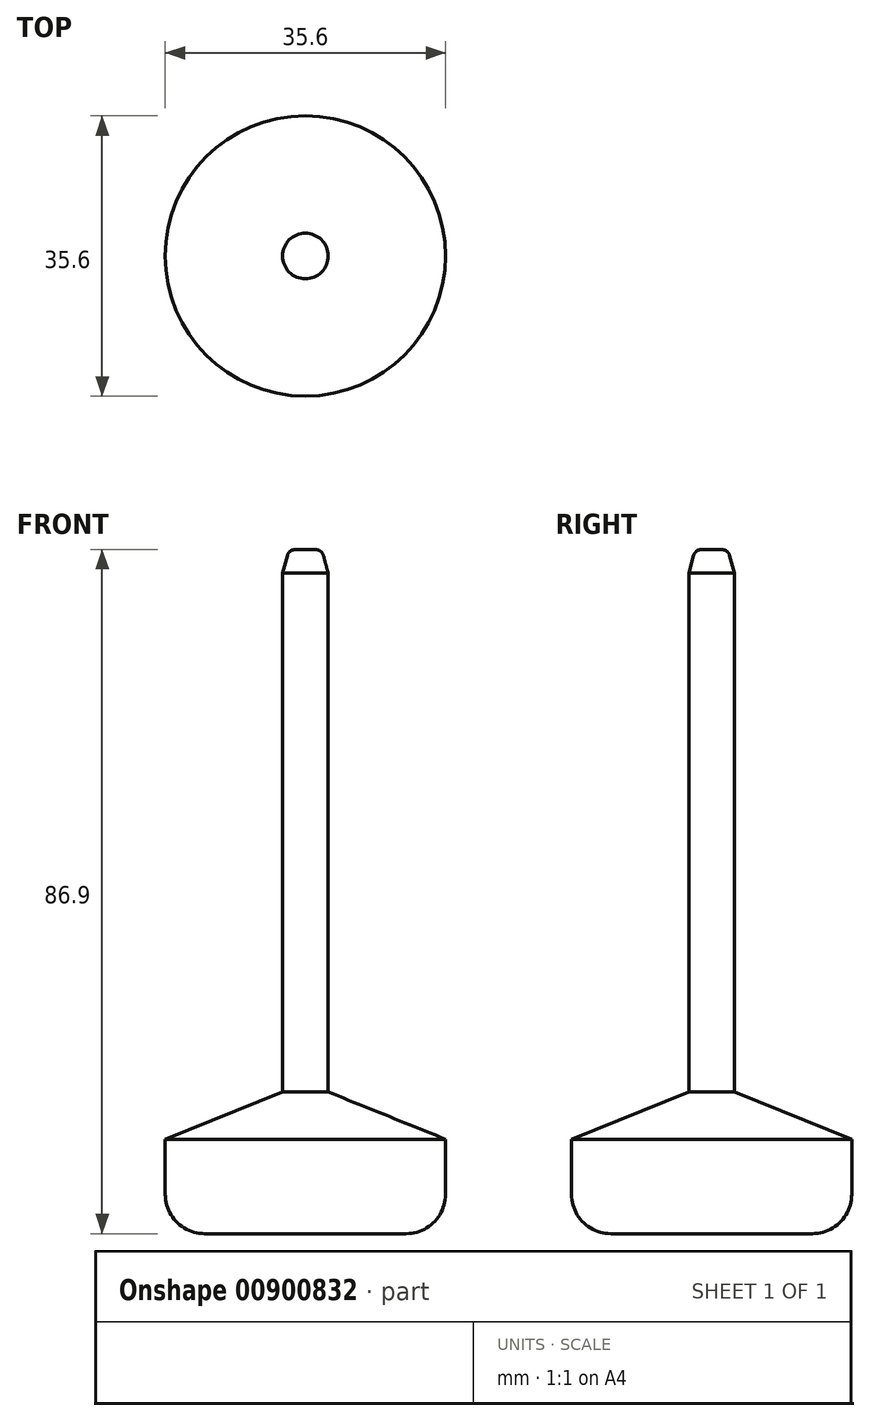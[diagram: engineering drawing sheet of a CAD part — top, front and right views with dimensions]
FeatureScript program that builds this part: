
annotation { "Feature Type Name" : "Feature", "Feature Type Description" : "" }
export const myFeature = defineFeature(function(context is Context, id is Id, definition is map)
    precondition{}
    {
        {
            var Q0;
            Q0=qCreatedBy(makeId("Top.planeOp"),FACE);
            var sketch = newSketch(context, id + "F0", { "sketchPlane" : qUnion([Q0])});
            skCircle(sketch, "E0", {"center": v(0, 0) * mm, "radius": 17.8 * mm});
            skSolve(sketch);
        }
        {
            var Q0;
            Q0=makeQuery(id+"F0.imprint","IMPRINT",FACE,{"disambiguationData":[TD([[makeQuery(id+"F0.imprint","IMPRINT",EDGE,{"derivedFrom":sQuery(id+"F0.wireOp",EDGE,"E0")}),1.0]])]});
            cPlane(context, id + "F1", {"entities" : qUnion([Q0]), "cplaneType" : CPlaneType.OFFSET, "offset" : 18 * mm, "width" : 150 * mm, "height" : 150 * mm});
        }
        {
            var Q0;
            Q0=qCreatedBy(id+"F1.planeOp",FACE);
            var sketch = newSketch(context, id + "F2", { "sketchPlane" : qUnion([Q0])});
            skCircle(sketch, "E1", {"center": v(0, 0) * mm, "radius": 2.9 * mm});
            skSolve(sketch);
        }
        {
            var Q0;
            Q0 = qSketchRegion(id + "F0", true);
            extrude(context, id + "F3", {"entities" : qUnion([Q0]), "depth" : 12 * mm, "offsetDistance" : 25 * mm});
        }
        {
            var Q0;
            Q0 = qSketchRegion(id + "F2", true);
            extrude(context, id + "F4", {"entities" : qUnion([Q0]), "depth" : 65.9 * mm, "offsetDistance" : 25 * mm});
        }
        {
            var Q0;
            Q0=makeQuery(id+"F4.opExtrude","CAP_FACE",FACE,{"disambiguationData":[OSD([sQuery(id+"F2.wireOp",EDGE,"E1")])],"isStart":true});
            var Q1;
            Q1=makeQuery(id+"F3.opExtrude","CAP_FACE",FACE,{"disambiguationData":[OSD([sQuery(id+"F0.wireOp",EDGE,"E0")])],"isStart":false});
            loft(context, id + "F5", {"sheetProfilesArray" : [{ "sheetProfileEntities" : qUnion([Q0]) }, { "sheetProfileEntities" : qUnion([Q1]) }]});
        }
        {
            var Q0;
            Q0=makeQuery(id+"F4.opExtrude","CAP_FACE",FACE,{"disambiguationData":[OSD([sQuery(id+"F2.wireOp",EDGE,"E1")])],"isStart":false});
            cPlane(context, id + "F6", {"entities" : qUnion([Q0]), "cplaneType" : CPlaneType.OFFSET, "offset" : 3 * mm, "width" : 150 * mm, "height" : 150 * mm});
        }
        {
            var Q0;
            Q0=qCreatedBy(id+"F6.planeOp",FACE);
            var sketch = newSketch(context, id + "F7", { "sketchPlane" : qUnion([Q0])});
            skCircle(sketch, "E2", {"center": v(0, 0) * mm, "radius": 2.08 * mm});
            skSolve(sketch);
        }
        {
            var Q1;
            Q1=makeQuery(id+"F4.opExtrude","CAP_FACE",FACE,{"disambiguationData":[OSD([sQuery(id+"F2.wireOp",EDGE,"E1")])],"isStart":false});
            var Q2;
            Q2=makeQuery(id+"F7.imprint","IMPRINT",FACE,{"disambiguationData":[TD([[makeQuery(id+"F7.imprint","IMPRINT",EDGE,{"derivedFrom":sQuery(id+"F7.wireOp",EDGE,"E2")}),1.0]])]});
            loft(context, id + "F8", {"operationType" : NewBodyOperationType.ADD, "sheetProfilesArray" : [{ "sheetProfileEntities" : qUnion([Q1]) }, { "sheetProfileEntities" : qUnion([Q2]) }]});
        }
        {
            var Q0;
            Q0=makeQuery(id+"F8.opLoft","MID_CAP_EDGE",EDGE,{"disambiguationData":[OSD([sQuery(id+"F7.wireOp",EDGE,"E2")])],"capPos":1.0});
            fillet(context, id + "F9", {"entities" : qUnion([Q0]), "radius" : 1 * mm, "tangentPropagation" : true, "allowEdgeOverflow" : false});
        }
        {
            var Q0;
            Q0=makeQuery(id+"F3.opExtrude","CAP_EDGE",EDGE,{"disambiguationData":[OSD([sQuery(id+"F0.wireOp",EDGE,"E0")])],"isStart":true});
            fillet(context, id + "F10", {"entities" : qUnion([Q0]), "radius" : 5 * mm, "tangentPropagation" : true, "allowEdgeOverflow" : false});
        }
    });
